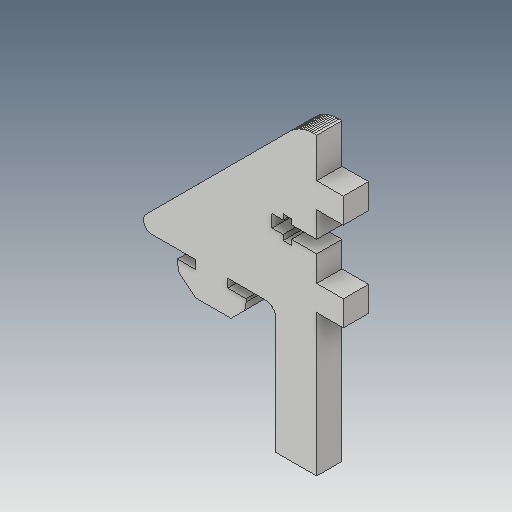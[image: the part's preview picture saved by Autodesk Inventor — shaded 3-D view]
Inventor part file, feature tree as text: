
AUTODESK INVENTOR PART (.ipt)
format: ipt  version: 2017 (Build 210142000, 142)  size: 361,984 bytes
history: native  units: mm
features: other x3, sketch x1
ambient origin geometry x8: Origin, YZ Plane, XZ Plane, XY Plane, X Axis, Y Axis, Z Axis, Center Point
bodies: Solid1 (feature_tree)
feature tree (4):
  other  "Y-Motor-Brace_MIR.ipt"
  other  "Solid1::Y-Motor-Brace_MIR.ipt"
  other  "TaggingFeature1"
  sketch  "Sketch1"  dims[d0=10.0mm]
